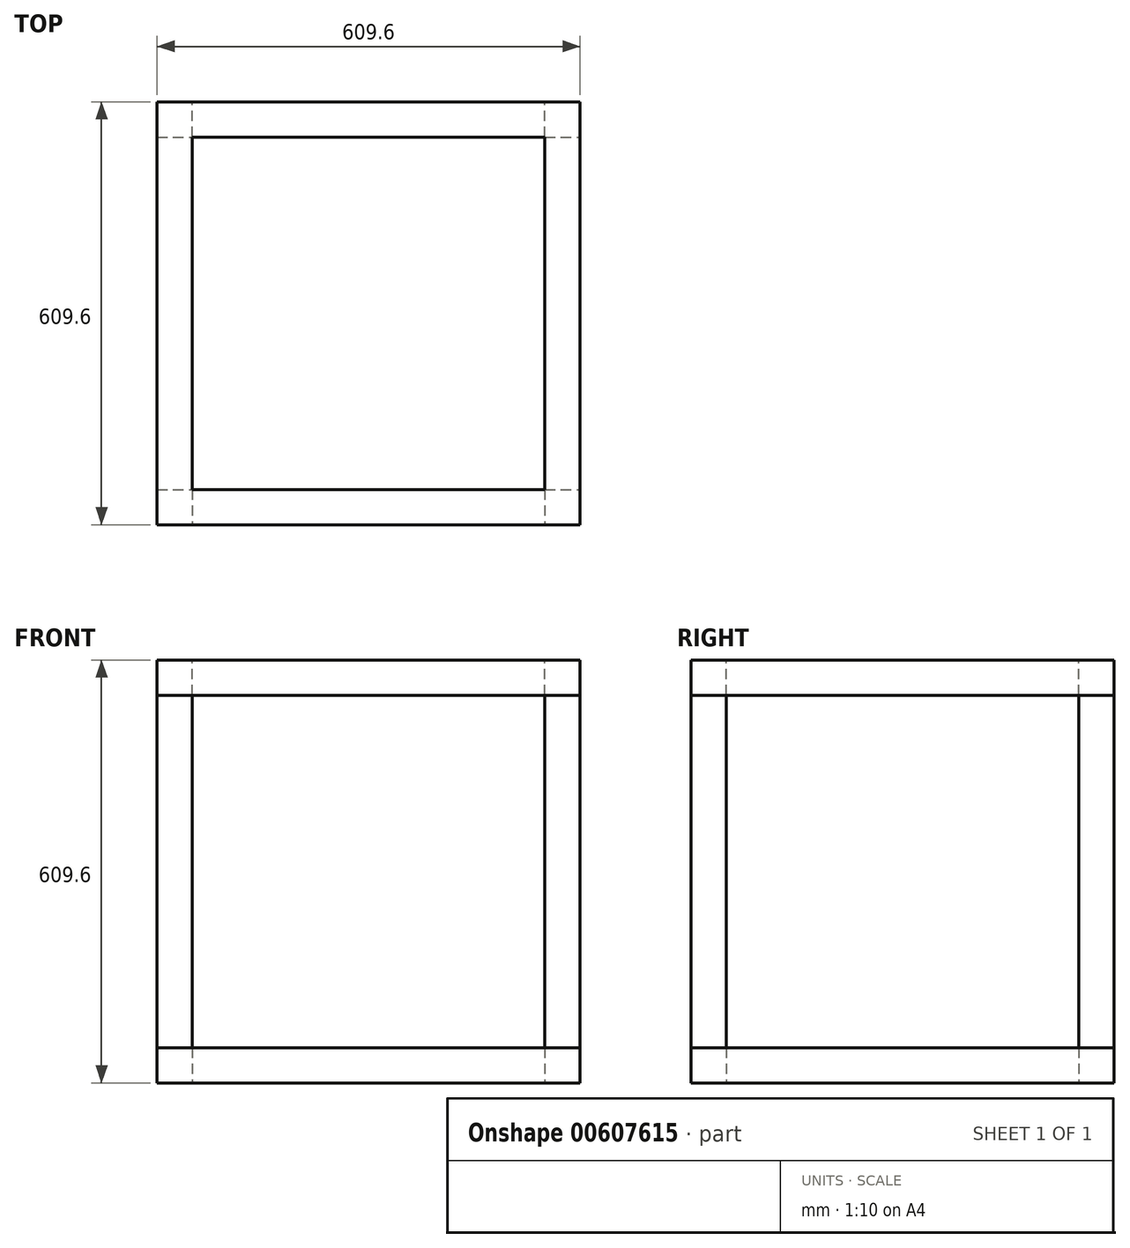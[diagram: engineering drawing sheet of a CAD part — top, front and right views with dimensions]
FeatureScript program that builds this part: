
annotation { "Feature Type Name" : "Feature", "Feature Type Description" : "" }
export const myFeature = defineFeature(function(context is Context, id is Id, definition is map)
    precondition{}
    {
        {
            var Q0;
            Q0=qCreatedBy(makeId("Top.planeOp"),FACE);
            var sketch = newSketch(context, id + "F0", { "sketchPlane" : qUnion([Q0])});
            skLineSegment(sketch, "E0.bottom", {"start": v(-304.8, -304.8) * mm, "end": v(304.8, -304.8) * mm});
            skLineSegment(sketch, "E0.top", {"start": v(-304.8, 304.8) * mm, "end": v(304.8, 304.8) * mm});
            skLineSegment(sketch, "E0.left", {"start": v(-304.8, -304.8) * mm, "end": v(-304.8, 304.8) * mm});
            skLineSegment(sketch, "E0.right", {"start": v(304.8, -304.8) * mm, "end": v(304.8, 304.8) * mm});
            skPoint(sketch, "E0.middle", {"position": v(0, 0) * mm});
            skLineSegment(sketch, "E1.bottom", {"start": v(-254, -254) * mm, "end": v(254, -254) * mm});
            skLineSegment(sketch, "E1.top", {"start": v(-254, 254) * mm, "end": v(254, 254) * mm});
            skLineSegment(sketch, "E1.left", {"start": v(-254, -254) * mm, "end": v(-254, 254) * mm});
            skLineSegment(sketch, "E1.right", {"start": v(254, -254) * mm, "end": v(254, 254) * mm});
            skSolve(sketch);
        }
        {
            var Q0;
            Q0=makeQuery(id+"F0.imprint","IMPRINT",FACE,{"disambiguationData":[TD([[makeQuery(id+"F0.imprint","IMPRINT",EDGE,{"derivedFrom":sQuery(id+"F0.wireOp",EDGE,"E0.bottom")}),1.0]])]});
            extrude(context, id + "F1", {"entities" : qUnion([Q0]), "depth" : 50.8 * mm, "offsetDistance" : 25.4 * mm});
        }
        {
            var Q0;
            Q0=makeQuery(id+"F1.opExtrude","CAP_FACE",FACE,{"disambiguationData":[OSD([sQuery(id+"F0.wireOp",EDGE,"E0.bottom"),sQuery(id+"F0.wireOp",EDGE,"E0.top"),sQuery(id+"F0.wireOp",EDGE,"E0.left"),sQuery(id+"F0.wireOp",EDGE,"E0.right"),sQuery(id+"F0.wireOp",EDGE,"E1.bottom"),sQuery(id+"F0.wireOp",EDGE,"E1.top"),sQuery(id+"F0.wireOp",EDGE,"E1.left"),sQuery(id+"F0.wireOp",EDGE,"E1.right")])],"isStart":false});
            cPlane(context, id + "F2", {"entities" : qUnion([Q0]), "cplaneType" : CPlaneType.OFFSET, "offset" : 254 * mm, "width" : 152.4 * mm, "height" : 152.4 * mm});
        }
        {
            var Q0;
            Q0=makeQuery(id+"F1.opExtrude","SWEPT_BODY",BODY,{"disambiguationData":[OSD([sQuery(id+"F0.wireOp",EDGE,"E0.bottom"),sQuery(id+"F0.wireOp",EDGE,"E0.top"),sQuery(id+"F0.wireOp",EDGE,"E0.left"),sQuery(id+"F0.wireOp",EDGE,"E0.right"),sQuery(id+"F0.wireOp",EDGE,"E1.bottom"),sQuery(id+"F0.wireOp",EDGE,"E1.top"),sQuery(id+"F0.wireOp",EDGE,"E1.left"),sQuery(id+"F0.wireOp",EDGE,"E1.right")])]});
            var Q1;
            Q1=qCreatedBy(id+"F2.planeOp",FACE);
            mirror(context, id + "F3", {"entities" : qUnion([Q0]), "mirrorPlane" : qUnion([Q1])});
        }
        {
            var Q0;
            Q0=makeQuery(id+"F3.opPattern","COPY",FACE,{"derivedFrom":makeQuery(id+"F1.opExtrude","SWEPT_FACE",FACE,{"disambiguationData":[OSD([sQuery(id+"F0.wireOp",EDGE,"E0.bottom")])]}),"instanceName":"1"});
            var sketch = newSketch(context, id + "F4", { "sketchPlane" : qUnion([Q0])});
            skLineSegment(sketch, "E2.bottom", {"start": v(-304.8, 558.8) * mm, "end": v(-254, 558.8) * mm});
            skLineSegment(sketch, "E2.top", {"start": v(-304.8, 50.8) * mm, "end": v(-254, 50.8) * mm});
            skLineSegment(sketch, "E2.left", {"start": v(-304.8, 558.8) * mm, "end": v(-304.8, 50.8) * mm});
            skLineSegment(sketch, "E2.right", {"start": v(-254, 558.8) * mm, "end": v(-254, 50.8) * mm});
            skLineSegment(sketch, "E3", {"start": v(0, 488.3) * mm, "end": v(0, 380.1) * mm, "construction": true});
            skPoint(sketch, "E3.startSnap0", {"position": v(0, 558.8) * mm});
            skLineSegment(sketch, "E4.MirrorCS", {"start": v(254, 558.8) * mm, "end": v(254, 50.8) * mm});
            skLineSegment(sketch, "E5.MirrorCS", {"start": v(304.8, 558.8) * mm, "end": v(304.8, 50.8) * mm});
            skLineSegment(sketch, "E6.MirrorCS", {"start": v(304.8, 558.8) * mm, "end": v(254, 558.8) * mm});
            skLineSegment(sketch, "E7.MirrorCS", {"start": v(304.8, 50.8) * mm, "end": v(254, 50.8) * mm});
            skSolve(sketch);
        }
        {
            var Q0;
            Q0=makeQuery(id+"F4.imprint","IMPRINT",FACE,{"disambiguationData":[TD([[makeQuery(id+"F4.imprint","IMPRINT",EDGE,{"derivedFrom":sQuery(id+"F4.wireOp",EDGE,"E2.bottom")}),-1.0]])]});
            var Q1;
            Q1=makeQuery(id+"F4.imprint","IMPRINT",FACE,{"disambiguationData":[TD([[makeQuery(id+"F4.imprint","IMPRINT",EDGE,{"derivedFrom":sQuery(id+"F4.wireOp",EDGE,"E4.MirrorCS")}),1.0]])]});
            extrude(context, id + "F5", {"entities" : qUnion([Q0, Q1]), "oppositeDirection" : true, "depth" : 50.8 * mm, "offsetDistance" : 25.4 * mm});
        }
        {
            var Q0;
            Q0=makeQuery(id+"F3.opPattern","COPY",FACE,{"derivedFrom":makeQuery(id+"F1.opExtrude","SWEPT_FACE",FACE,{"disambiguationData":[OSD([sQuery(id+"F0.wireOp",EDGE,"E1.bottom")])]}),"instanceName":"1"});
            cPlane(context, id + "F6", {"entities" : qUnion([Q0]), "cplaneType" : CPlaneType.OFFSET, "offset" : 254 * mm, "width" : 152.4 * mm, "height" : 152.4 * mm});
        }
        {
            var Q0;
            Q0=makeQuery(id+"F5.opExtrude","SWEPT_BODY",BODY,{"disambiguationData":[OSD([sQuery(id+"F4.wireOp",EDGE,"E4.MirrorCS"),sQuery(id+"F4.wireOp",EDGE,"E5.MirrorCS"),sQuery(id+"F4.wireOp",EDGE,"E6.MirrorCS"),sQuery(id+"F4.wireOp",EDGE,"E7.MirrorCS")])]});
            var Q1;
            Q1=qCreatedBy(id+"F6.planeOp",FACE);
            mirror(context, id + "F7", {"entities" : qUnion([Q0]), "mirrorPlane" : qUnion([Q1])});
        }
        {
            var Q0;
            Q0=makeQuery(id+"F5.opExtrude","SWEPT_BODY",BODY,{"disambiguationData":[OSD([sQuery(id+"F4.wireOp",EDGE,"E2.bottom"),sQuery(id+"F4.wireOp",EDGE,"E2.top"),sQuery(id+"F4.wireOp",EDGE,"E2.left"),sQuery(id+"F4.wireOp",EDGE,"E2.right")])]});
            var Q1;
            Q1=qCreatedBy(id+"F6.planeOp",FACE);
            mirror(context, id + "F8", {"entities" : qUnion([Q0]), "mirrorPlane" : qUnion([Q1])});
        }
    });
